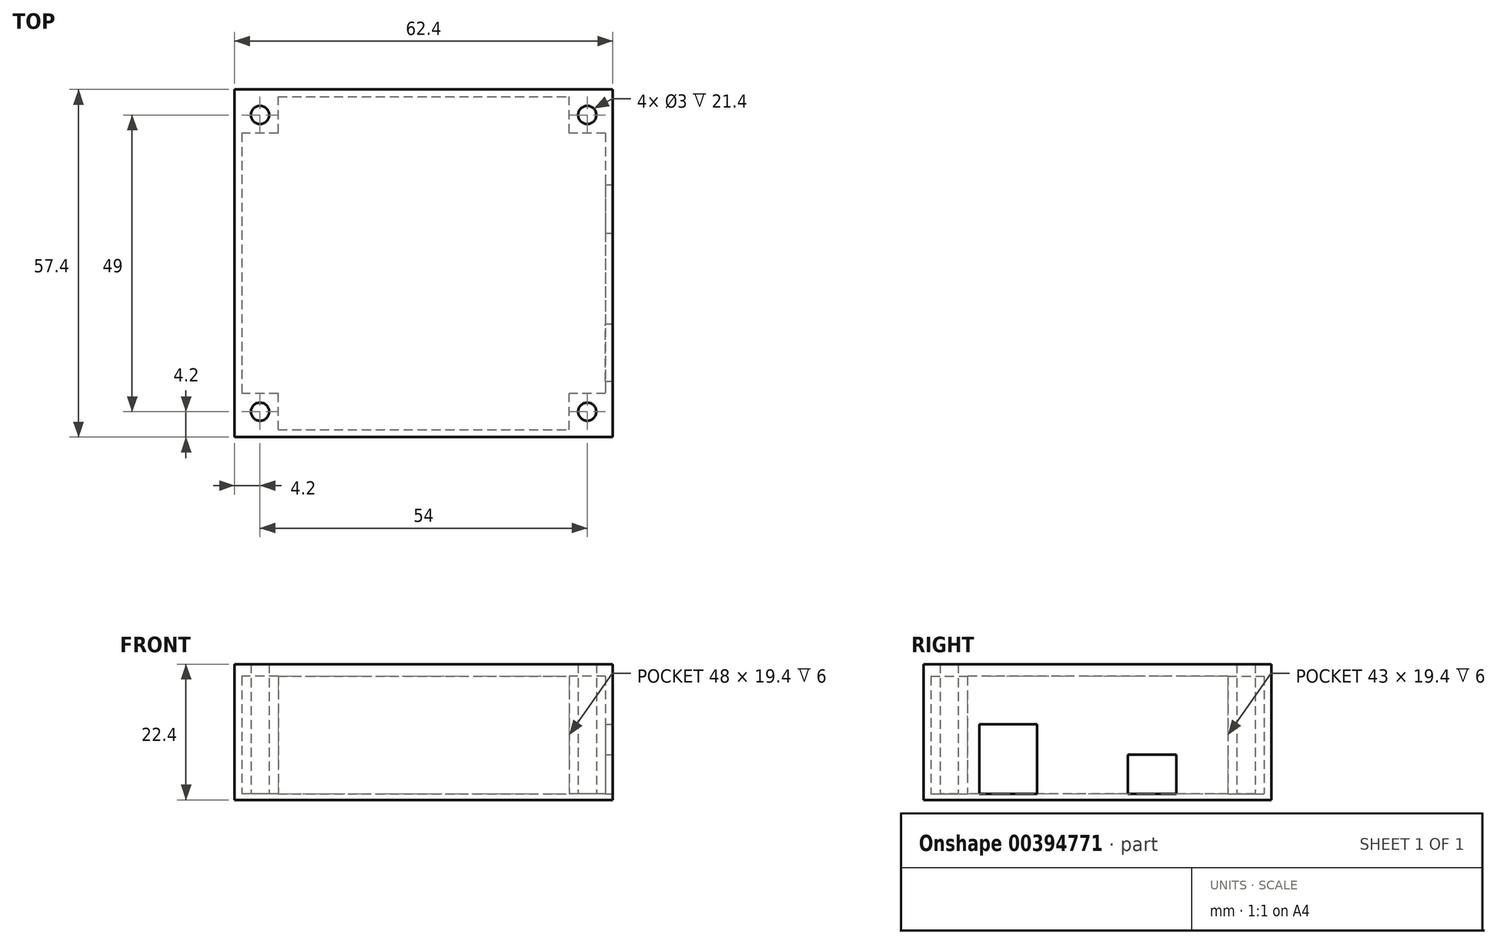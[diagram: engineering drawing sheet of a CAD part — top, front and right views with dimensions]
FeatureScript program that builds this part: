
annotation { "Feature Type Name" : "Feature", "Feature Type Description" : "" }
export const myFeature = defineFeature(function(context is Context, id is Id, definition is map)
    precondition{}
    {
        {
            var Q0;
            Q0=qCreatedBy(makeId("Top.planeOp"),FACE);
            var sketch = newSketch(context, id + "F0", { "sketchPlane" : qUnion([Q0])});
            skLineSegment(sketch, "E0.bottom", {"start": v(-30, 22.5) * mm, "end": v(30, 22.5) * mm});
            skLineSegment(sketch, "E0.top", {"start": v(-30, -32.5) * mm, "end": v(30, -32.5) * mm});
            skLineSegment(sketch, "E0.left", {"start": v(-30, 22.5) * mm, "end": v(-30, -32.5) * mm});
            skLineSegment(sketch, "E0.right", {"start": v(30, 22.5) * mm, "end": v(30, -32.5) * mm});
            skLineSegment(sketch, "E1.0", {"start": v(-31.2, 23.7) * mm, "end": v(-31.2, -33.7) * mm});
            skLineSegment(sketch, "E1.1", {"start": v(-31.2, 23.7) * mm, "end": v(31.2, 23.7) * mm});
            skLineSegment(sketch, "E1.2", {"start": v(31.2, 23.7) * mm, "end": v(31.2, -33.7) * mm});
            skLineSegment(sketch, "E1.3", {"start": v(-31.2, -33.7) * mm, "end": v(31.2, -33.7) * mm});
            skCircle(sketch, "E2", {"center": v(27, -29.5) * mm, "radius": 1.5 * mm});
            skLineSegment(sketch, "E3.bottom", {"start": v(30, -32.5) * mm, "end": v(24, -32.5) * mm});
            skLineSegment(sketch, "E3.top", {"start": v(30, -26.5) * mm, "end": v(24, -26.5) * mm});
            skLineSegment(sketch, "E3.left", {"start": v(30, -32.5) * mm, "end": v(30, -26.5) * mm});
            skLineSegment(sketch, "E3.right", {"start": v(24, -32.5) * mm, "end": v(24, -26.5) * mm});
            skCircle(sketch, "E4", {"center": v(27, 19.5) * mm, "radius": 1.5 * mm});
            skLineSegment(sketch, "E5.bottom", {"start": v(30, 16.5) * mm, "end": v(24, 16.5) * mm});
            skLineSegment(sketch, "E5.top", {"start": v(30, 22.5) * mm, "end": v(24, 22.5) * mm});
            skLineSegment(sketch, "E5.left", {"start": v(30, 16.5) * mm, "end": v(30, 22.5) * mm});
            skLineSegment(sketch, "E5.right", {"start": v(24, 16.5) * mm, "end": v(24, 22.5) * mm});
            skCircle(sketch, "E6", {"center": v(-27, 19.5) * mm, "radius": 1.5 * mm});
            skLineSegment(sketch, "E7.bottom", {"start": v(-24, 16.5) * mm, "end": v(-30, 16.5) * mm});
            skLineSegment(sketch, "E7.top", {"start": v(-24, 22.5) * mm, "end": v(-30, 22.5) * mm});
            skLineSegment(sketch, "E7.left", {"start": v(-24, 16.5) * mm, "end": v(-24, 22.5) * mm});
            skLineSegment(sketch, "E7.right", {"start": v(-30, 16.5) * mm, "end": v(-30, 22.5) * mm});
            skCircle(sketch, "E8", {"center": v(-27, -29.5) * mm, "radius": 1.5 * mm});
            skLineSegment(sketch, "E9.bottom", {"start": v(-24, -32.5) * mm, "end": v(-30, -32.5) * mm});
            skLineSegment(sketch, "E9.top", {"start": v(-24, -26.5) * mm, "end": v(-30, -26.5) * mm});
            skLineSegment(sketch, "E9.left", {"start": v(-24, -32.5) * mm, "end": v(-24, -26.5) * mm});
            skLineSegment(sketch, "E9.right", {"start": v(-30, -32.5) * mm, "end": v(-30, -26.5) * mm});
            skSolve(sketch);
        }
        {
            var Q0;
            Q0=makeQuery(id+"F0.imprint","IMPRINT",FACE,{"disambiguationData":[TD([[makeQuery(id+"F0.imprint","IMPRINT",EDGE,{"derivedFrom":sQuery(id+"F0.wireOp",EDGE,"E0.bottom")}),1.0]])]});
            var Q1;
            Q1=makeQuery(id+"F0.imprint","IMPRINT",FACE,{"disambiguationData":[TD([[makeQuery(id+"F0.imprint","IMPRINT",EDGE,{"derivedFrom":sQuery(id+"F0.wireOp",EDGE,"E2")}),-1.0]])]});
            var Q2;
            Q2=makeQuery(id+"F0.imprint","IMPRINT",FACE,{"disambiguationData":[TD([[makeQuery(id+"F0.imprint","IMPRINT",EDGE,{"derivedFrom":sQuery(id+"F0.wireOp",EDGE,"E6")}),-1.0]])]});
            var Q3;
            Q3=makeQuery(id+"F0.imprint","IMPRINT",FACE,{"disambiguationData":[TD([[makeQuery(id+"F0.imprint","IMPRINT",EDGE,{"derivedFrom":sQuery(id+"F0.wireOp",EDGE,"E8")}),-1.0]])]});
            var Q4;
            Q4=makeQuery(id+"F0.imprint","IMPRINT",FACE,{"disambiguationData":[TD([[makeQuery(id+"F0.imprint","IMPRINT",EDGE,{"derivedFrom":sQuery(id+"F0.wireOp",EDGE,"E4")}),-1.0]])]});
            extrude(context, id + "F1", {"entities" : qUnion([Q0, Q1, Q2, Q3, Q4]), "depth" : 20 * mm});
        }
        {
            var Q0;
            Q0=qCreatedBy(makeId("Top.planeOp"),FACE);
            var sketch = newSketch(context, id + "F2", { "sketchPlane" : qUnion([Q0])});
            skLineSegment(sketch, "E10.bottom", {"start": v(31.2, 23.7) * mm, "end": v(-31.2, 23.7) * mm});
            skLineSegment(sketch, "E10.top", {"start": v(31.2, -33.7) * mm, "end": v(-31.2, -33.7) * mm});
            skLineSegment(sketch, "E10.left", {"start": v(31.2, 23.7) * mm, "end": v(31.2, -33.7) * mm});
            skLineSegment(sketch, "E10.right", {"start": v(-31.2, 23.7) * mm, "end": v(-31.2, -33.7) * mm});
            skLineSegment(sketch, "E11.bottom", {"start": v(-31.2, -33.7) * mm, "end": v(31.2, -33.7) * mm});
            skLineSegment(sketch, "E11.top", {"start": v(-31.2, 23.7) * mm, "end": v(31.2, 23.7) * mm});
            skLineSegment(sketch, "E11.left", {"start": v(-31.2, -33.7) * mm, "end": v(-31.2, 23.7) * mm});
            skLineSegment(sketch, "E11.right", {"start": v(31.2, -33.7) * mm, "end": v(31.2, 23.7) * mm});
            skSolve(sketch);
        }
        {
            var Q0;
            Q0 = qSketchRegion(id + "F2", true);
            extrude(context, id + "F3", {"entities" : qUnion([Q0]), "operationType" : NewBodyOperationType.ADD, "oppositeDirection" : true, "depth" : 1 * mm});
        }
        {
            var Q0;
            Q0=makeQuery(id+"F3.boolean.opBoolean","MERGE",FACE,{"derivedFrom":[makeQuery(id+"F1.opExtrude","SWEPT_FACE",FACE,{"disambiguationData":[OSD([sQuery(id+"F0.wireOp",EDGE,"E1.2")])]}),makeQuery(id+"F3.opExtrude","SWEPT_FACE",FACE,{"disambiguationData":[OSD([sQuery(id+"F2.wireOp",EDGE,"E11.right")])]})]});
            var sketch = newSketch(context, id + "F4", { "sketchPlane" : qUnion([Q0])});
            skLineSegment(sketch, "E12.bottom", {"start": v(0, 0) * mm, "end": v(8, 0) * mm});
            skLineSegment(sketch, "E12.top", {"start": v(0, 6.5) * mm, "end": v(8, 6.5) * mm});
            skLineSegment(sketch, "E12.left", {"start": v(0, 0) * mm, "end": v(0, 6.5) * mm});
            skLineSegment(sketch, "E12.right", {"start": v(8, 0) * mm, "end": v(8, 6.5) * mm});
            skLineSegment(sketch, "E13.bottom", {"start": v(-15, 0) * mm, "end": v(-24.5, 0) * mm});
            skLineSegment(sketch, "E13.top", {"start": v(-15, 11.5) * mm, "end": v(-24.5, 11.5) * mm});
            skLineSegment(sketch, "E13.left", {"start": v(-15, 0) * mm, "end": v(-15, 11.5) * mm});
            skLineSegment(sketch, "E13.right", {"start": v(-24.5, 0) * mm, "end": v(-24.5, 11.5) * mm});
            skSolve(sketch);
        }
        {
            var Q0;
            Q0=makeQuery(id+"F4.imprint","IMPRINT",FACE,{"disambiguationData":[TD([[makeQuery(id+"F4.imprint","IMPRINT",EDGE,{"derivedFrom":sQuery(id+"F4.wireOp",EDGE,"E13.bottom")}),-1.0]])]});
            var Q1;
            Q1=makeQuery(id+"F4.imprint","IMPRINT",FACE,{"disambiguationData":[TD([[makeQuery(id+"F4.imprint","IMPRINT",EDGE,{"derivedFrom":sQuery(id+"F4.wireOp",EDGE,"E12.bottom")}),1.0]])]});
            extrude(context, id + "F5", {"entities" : qUnion([Q0, Q1]), "operationType" : NewBodyOperationType.REMOVE, "endBound" : BoundingType.UP_TO_NEXT, "oppositeDirection" : true, "depth" : 25 * mm});
        }
        {
            var Q0;
            Q0=makeQuery(id+"F1.opExtrude","CAP_FACE",FACE,{"disambiguationData":[OSD([sQuery(id+"F0.wireOp",EDGE,"E0.bottom"),sQuery(id+"F0.wireOp",EDGE,"E0.top"),sQuery(id+"F0.wireOp",EDGE,"E0.left"),sQuery(id+"F0.wireOp",EDGE,"E0.right"),sQuery(id+"F0.wireOp",EDGE,"E1.0"),sQuery(id+"F0.wireOp",EDGE,"E1.1"),sQuery(id+"F0.wireOp",EDGE,"E1.2"),sQuery(id+"F0.wireOp",EDGE,"E1.3"),sQuery(id+"F0.wireOp",EDGE,"E2"),sQuery(id+"F0.wireOp",EDGE,"E3.top"),sQuery(id+"F0.wireOp",EDGE,"E3.right"),sQuery(id+"F0.wireOp",EDGE,"E4"),sQuery(id+"F0.wireOp",EDGE,"E5.bottom"),sQuery(id+"F0.wireOp",EDGE,"E5.right"),sQuery(id+"F0.wireOp",EDGE,"E6"),sQuery(id+"F0.wireOp",EDGE,"E7.bottom"),sQuery(id+"F0.wireOp",EDGE,"E7.left"),sQuery(id+"F0.wireOp",EDGE,"E8"),sQuery(id+"F0.wireOp",EDGE,"E9.top"),sQuery(id+"F0.wireOp",EDGE,"E9.left")])],"isStart":false});
            var sketch = newSketch(context, id + "F6", { "sketchPlane" : qUnion([Q0])});
            skLineSegment(sketch, "E14.bottom", {"start": v(-31.2, 23.7) * mm, "end": v(31.2, 23.7) * mm});
            skLineSegment(sketch, "E14.top", {"start": v(-31.2, -33.7) * mm, "end": v(31.2, -33.7) * mm});
            skLineSegment(sketch, "E14.left", {"start": v(-31.2, 23.7) * mm, "end": v(-31.2, -33.7) * mm});
            skLineSegment(sketch, "E14.right", {"start": v(31.2, 23.7) * mm, "end": v(31.2, -33.7) * mm});
            skCircle(sketch, "E15", {"center": v(-27, 19.5) * mm, "radius": 1.5 * mm});
            skCircle(sketch, "E16", {"center": v(27, 19.5) * mm, "radius": 1.5 * mm});
            skCircle(sketch, "E17", {"center": v(27, -29.5) * mm, "radius": 1.5 * mm});
            skCircle(sketch, "E18", {"center": v(-27, -29.5) * mm, "radius": 1.5 * mm});
            skSolve(sketch);
        }
        {
            var Q0;
            Q0=makeQuery(id+"F6.imprint","IMPRINT",FACE,{"disambiguationData":[TD([[makeQuery(id+"F6.imprint","IMPRINT",EDGE,{"derivedFrom":makeQuery(id+"F1.opExtrude","CAP_EDGE",EDGE,{"disambiguationData":[OSD([sQuery(id+"F0.wireOp",EDGE,"E0.bottom")])],"isStart":false})}),-1.0]])]});
            extrude(context, id + "F7", {"entities" : qUnion([Q0]), "oppositeDirection" : true, "depth" : .6 * mm});
        }
        {
            var Q0;
            Q0=makeQuery(id+"F6.imprint","IMPRINT",FACE,{"disambiguationData":[TD([[makeQuery(id+"F6.imprint","IMPRINT",EDGE,{"derivedFrom":sQuery(id+"F6.wireOp",EDGE,"E14.bottom")}),-1.0]])]});
            var Q1;
            Q1=makeQuery(id+"F6.imprint","IMPRINT",FACE,{"disambiguationData":[TD([[makeQuery(id+"F6.imprint","IMPRINT",EDGE,{"derivedFrom":makeQuery(id+"F1.opExtrude","CAP_EDGE",EDGE,{"disambiguationData":[OSD([sQuery(id+"F0.wireOp",EDGE,"E0.bottom")])],"isStart":false})}),-1.0]])]});
            extrude(context, id + "F8", {"entities" : qUnion([Q0, Q1]), "operationType" : NewBodyOperationType.ADD, "depth" : 1.4 * mm});
        }
    });
